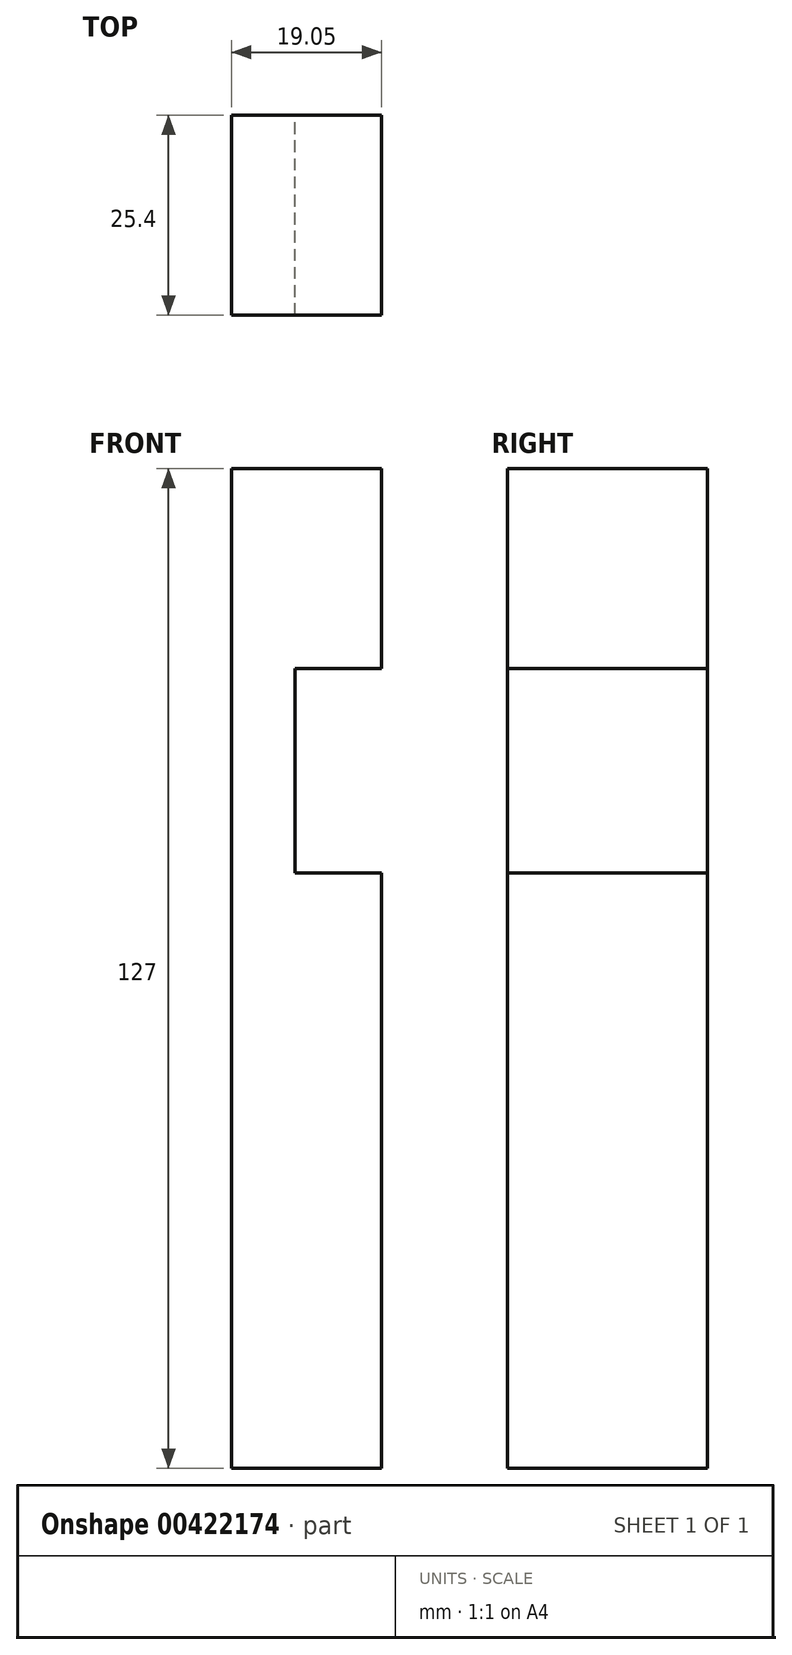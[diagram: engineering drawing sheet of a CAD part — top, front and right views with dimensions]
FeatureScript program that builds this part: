
annotation { "Feature Type Name" : "Feature", "Feature Type Description" : "" }
export const myFeature = defineFeature(function(context is Context, id is Id, definition is map)
    precondition{}
    {
        {
            var Q0;
            Q0=qCreatedBy(makeId("Front.planeOp"),FACE);
            var sketch = newSketch(context, id + "F0", { "sketchPlane" : qUnion([Q0])});
            skLineSegment(sketch, "E0", {"start": v(-57.42, 73.82) * mm, "end": v(-57.42, -53.18) * mm});
            skPoint(sketch, "E1.orphan", {"position": v(23.28, 61.66) * mm});
            skPoint(sketch, "E2.end.orphan", {"position": v(23.28, 71.18) * mm});
            skPoint(sketch, "E2.start.orphan", {"position": v(23.28, 80.7) * mm});
            skPoint(sketch, "E3.visualSharp", {"position": v(18.78, -53.18) * mm});
            skArc(sketch, "E3.filletArc", {"start": v(17.15, -53.18) * mm, "mid": v(18.3, -52.7) * mm, "end": v(18.78, -51.55) * mm});
            skPoint(sketch, "E4.visualSharp", {"position": v(18.78, 73.82) * mm});
            skLineSegment(sketch, "E5", {"start": v(18.78, -51.55) * mm, "end": v(18.78, -53.18) * mm});
            skLineSegment(sketch, "E6", {"start": v(-57.42, -53.18) * mm, "end": v(-38.37, -53.18) * mm});
            skPoint(sketch, "E7.end.orphan", {"position": v(-38.37, 65.75) * mm});
            skPoint(sketch, "E8.start.orphan", {"position": v(-38.37, 14.95) * mm});
            skLineSegment(sketch, "E9", {"start": v(-57.42, 73.82) * mm, "end": v(-38.37, 73.82) * mm});
            skLineSegment(sketch, "E10", {"start": v(-38.37, 73.82) * mm, "end": v(-38.37, 48.42) * mm});
            skLineSegment(sketch, "E11", {"start": v(-38.37, -53.18) * mm, "end": v(-38.37, -27.78) * mm});
            skLineSegment(sketch, "E12", {"start": v(-38.37, -27.78) * mm, "end": v(-38.37, 7.03) * mm});
            skLineSegment(sketch, "E13", {"start": v(-38.37, 7.03) * mm, "end": v(-38.37, 22.47) * mm});
            skLineSegment(sketch, "E14", {"start": v(-38.37, 22.47) * mm, "end": v(-49.37, 22.47) * mm});
            skLineSegment(sketch, "E15", {"start": v(-38.37, 48.42) * mm, "end": v(-49.37, 48.42) * mm});
            skLineSegment(sketch, "E16", {"start": v(-49.37, 20.23) * mm, "end": v(-49.37, 48.42) * mm});
            skSolve(sketch);
        }
        {
            var Q0;
            Q0=makeQuery(id+"F0.imprint","IMPRINT",FACE,{"disambiguationData":[TD([[makeQuery(id+"F0.imprint","IMPRINT",EDGE,{"derivedFrom":sQuery(id+"F0.wireOp",EDGE,"E0")}),1.0]])]});
            extrude(context, id + "F1", {"entities" : qUnion([Q0]), "depth" : 25.4 * mm});
        }
    });
